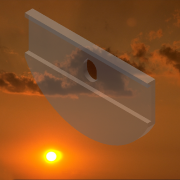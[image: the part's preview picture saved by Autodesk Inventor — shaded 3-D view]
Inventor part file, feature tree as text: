
AUTODESK INVENTOR PART (.ipt)
format: ipt  version: 2015 SP1 (Build 190203100, 203)  size: 162,816 bytes
history: native  units: in
note: dims shown in document units (in); Inventor stores cm internally (conversion verified against a paired STEP export)
features: extrude x4, sketch x4
ambient origin geometry x8: Origin, YZ Plane, XZ Plane, XY Plane, X Axis, Y Axis, Z Axis, Center Point
bodies: Solid1 (feature_tree)
feature tree (8):
  extrude  "Extrusion1"  Depth=8.0in
  extrude  "Extrusion2"  Depth=0.25in
  extrude  "Extrusion3"  Depth=0.25in TaperAngle=0.0deg
  extrude  "Extrusion4"  Depth=0.5in TaperAngle=0.0deg
  sketch  "Sketch1"  dims[d0=2.5in d1=8.0in]
  sketch  "Sketch2"  dims[d2=0.5in d3=0.0in d4=0.25in]
  sketch  "Sketch3"  dims[d5=0.25in d6=0.25in d7=0.0in]
  sketch  "Sketch4"  dims[d8=2.0in d9=0.5in d10=0.0in d11=4.0in d12=4.0in d13=0.875in d14=0.3in d15=0.875in d16=1.0in d17=0.5in d18=0.0in]
